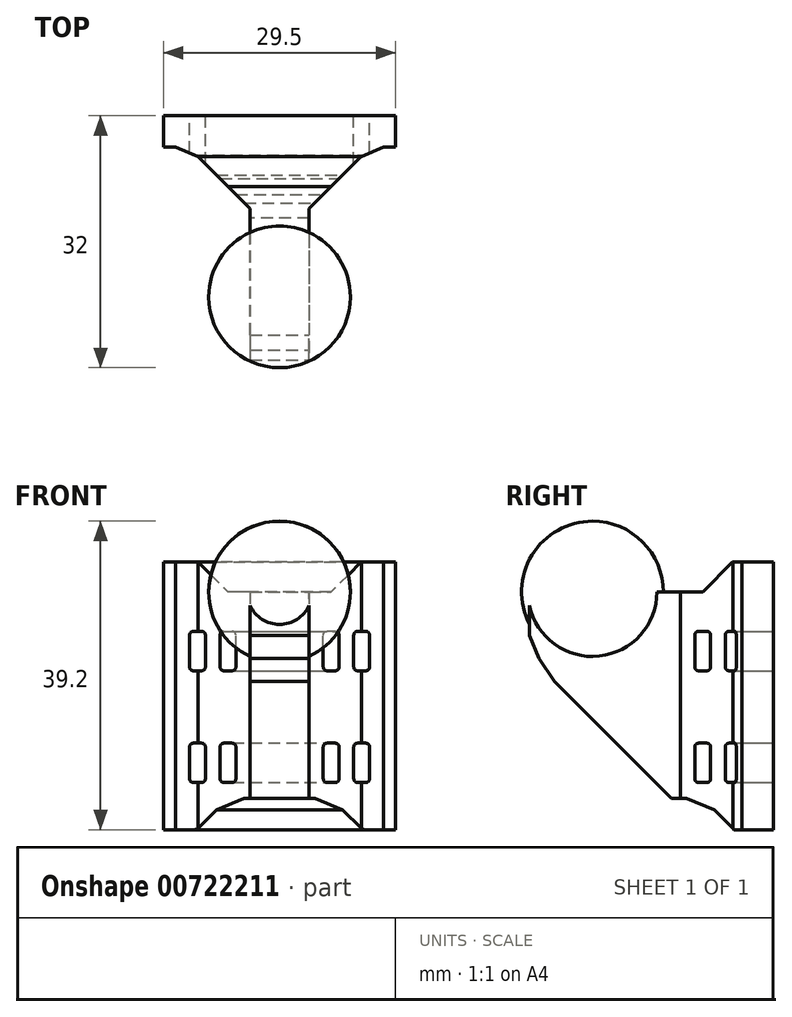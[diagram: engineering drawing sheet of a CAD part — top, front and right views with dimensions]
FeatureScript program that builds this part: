
annotation { "Feature Type Name" : "Feature", "Feature Type Description" : "" }
export const myFeature = defineFeature(function(context is Context, id is Id, definition is map)
    precondition{}
    {
        {
            var Q0;
            Q0=qCreatedBy(makeId("Top.planeOp"),FACE);
            var sketch = newSketch(context, id + "F0", { "sketchPlane" : qUnion([Q0])});
            skLineSegment(sketch, "E0", {"start": v(-34.8, 0) * mm, "end": v(28.46, 0) * mm, "construction": true});
            skArc(sketch, "E1", {"start": v(9, 0) * mm, "mid": v(0, 9) * mm, "end": v(-9, 0) * mm});
            skLineSegment(sketch, "E2", {"start": v(-9, 0) * mm, "end": v(9, 0) * mm});
            skSolve(sketch);
        }
        {
            var Q0;
            Q0 = qSketchRegion(id + "F0", true);
            var Q1;
            Q1=sQuery(id+"F0.wireOp",EDGE,"E0");
            revolve(context, id + "F1", {"surfaceOperationType" : NewSurfaceOperationType.NEW, "entities" : qUnion([Q0]), "axis" : qUnion([Q1]), "revolveType" : RevolveType.FULL});
        }
        {
            var Q0;
            Q0=qCreatedBy(makeId("Front.planeOp"),FACE);
            var sketch = newSketch(context, id + "F2", { "sketchPlane" : qUnion([Q0])});
            skLineSegment(sketch, "E3.bottom", {"start": v(-3.75, 0) * mm, "end": v(3.75, 0) * mm});
            skLineSegment(sketch, "E3.top", {"start": v(-3.75, -26.2) * mm, "end": v(3.75, -26.2) * mm});
            skLineSegment(sketch, "E3.left", {"start": v(-3.75, 0) * mm, "end": v(-3.75, -26.2) * mm});
            skLineSegment(sketch, "E3.right", {"start": v(3.75, 0) * mm, "end": v(3.75, -26.2) * mm});
            skPoint(sketch, "E3.middle", {"position": v(0, -13.1) * mm});
            skSolve(sketch);
        }
        {
            var Q0;
            Q0 = qSketchRegion(id + "F2", true);
            extrude(context, id + "F3", {"entities" : qUnion([Q0]), "operationType" : NewBodyOperationType.ADD, "oppositeDirection" : true, "depth" : 19 * mm, "offsetDistance" : 25 * mm, "hasSecondDirection" : true, "secondDirectionOppositeDirection" : false, "secondDirectionDepth" : 8 * mm});
        }
        {
            var Q0;
            {var subQ0=sQuery(id+"F2.wireOp",EDGE,"E3.top");Q0=makeQuery(id+"F11.opBoolean","MERGE",FACE,{"derivedFrom":[makeQuery(id+"F3.opExtrude","SWEPT_FACE",FACE,{"disambiguationData":[OSD([subQ0])]}),makeQuery(id+"F7.opExtrude","SWEPT_FACE",FACE,{"disambiguationData":[OSD([subQ0])]}),makeQuery(id+"F9.opExtrude","SWEPT_FACE",FACE,{"disambiguationData":[OSD([subQ0,sQuery(id+"F2.wireOp",EDGE,"E3.left")])]}),makeQuery(id+"F10.opExtrude","SWEPT_FACE",FACE,{"disambiguationData":[OSD([subQ0,sQuery(id+"F2.wireOp",EDGE,"E3.right")])]})]});}
            var sketch = newSketch(context, id + "F4", { "sketchPlane" : qUnion([Q0])});
            skLineSegment(sketch, "E4", {"start": v(-14.75, -19) * mm, "end": v(14.75, -19) * mm});
            skLineSegment(sketch, "E5", {"start": v(14.75, -19) * mm, "end": v(14.75, -23) * mm});
            skLineSegment(sketch, "E6", {"start": v(14.75, -23) * mm, "end": v(-14.75, -23) * mm});
            skLineSegment(sketch, "E7", {"start": v(-14.75, -23) * mm, "end": v(-14.75, -19) * mm});
            skSolve(sketch);
        }
        {
            var Q0;
            Q0=makeQuery(id+"F3.opExtrude","CAP_EDGE",EDGE,{"disambiguationData":[OSD([sQuery(id+"F2.wireOp",EDGE,"E3.top")])],"isStart":true});
            chamfer(context, id + "F5", {"entities" : qUnion([Q0]), "width" : 18 * mm, "tangentPropagation" : true});
        }
        {
            var Q0;
            {var subQ0=sQuery(id+"F2.wireOp",EDGE,"E3.top");Q0=makeQuery(id+"F5.opChamfer","BLEND_EDGE",EDGE,{"blendedFrom":[makeQuery(id+"F3.opExtrude","CAP_EDGE",EDGE,{"disambiguationData":[OSD([subQ0])],"isStart":true}),makeQuery(id+"F3.opExtrude","CAP_FACE",FACE,{"disambiguationData":[OSD([sQuery(id+"F2.wireOp",EDGE,"E3.bottom"),subQ0,sQuery(id+"F2.wireOp",EDGE,"E3.left"),sQuery(id+"F2.wireOp",EDGE,"E3.right")])],"isStart":true})],"blendedInto":[makeQuery(id+"F3.opExtrude","CAP_FACE",FACE,{"disambiguationData":[OSD([sQuery(id+"F2.wireOp",EDGE,"E3.bottom"),subQ0,sQuery(id+"F2.wireOp",EDGE,"E3.left"),sQuery(id+"F2.wireOp",EDGE,"E3.right")])],"isStart":true})]});}
            chamfer(context, id + "F6", {"entities" : qUnion([Q0]), "width" : 6.5 * mm, "tangentPropagation" : true});
        }
        {
            var Q0;
            Q0=makeQuery(id+"F3.opExtrude","CAP_FACE",FACE,{"disambiguationData":[OSD([sQuery(id+"F2.wireOp",EDGE,"E3.bottom"),sQuery(id+"F2.wireOp",EDGE,"E3.top"),sQuery(id+"F2.wireOp",EDGE,"E3.left"),sQuery(id+"F2.wireOp",EDGE,"E3.right")])],"isStart":false});
            extrude(context, id + "F7", {"entities" : qUnion([Q0]), "depth" : 4 * mm, "offsetDistance" : 25 * mm});
        }
        {
            var Q0;
            Q0=makeQuery(id+"F7.opExtrude","CAP_EDGE",EDGE,{"disambiguationData":[OSD([sQuery(id+"F2.wireOp",EDGE,"E3.bottom")])],"isStart":false});
            chamfer(context, id + "F8", {"entities" : qUnion([Q0]), "chamferType" : ChamferType.OFFSET_ANGLE, "width" : 3 * mm, "oppositeDirection" : false, "angle" : 70 * degree, "tangentPropagation" : true});
        }
        {
            var Q0;
            Q0=makeQuery(id+"F7.opExtrude","SWEPT_FACE",FACE,{"disambiguationData":[OSD([sQuery(id+"F2.wireOp",EDGE,"E3.left")])]});
            extrude(context, id + "F9", {"entities" : qUnion([Q0]), "depth" : 11 * mm, "offsetDistance" : 25 * mm});
        }
        {
            var Q0;
            Q0=makeQuery(id+"F7.opExtrude","SWEPT_FACE",FACE,{"disambiguationData":[OSD([sQuery(id+"F2.wireOp",EDGE,"E3.right")])]});
            extrude(context, id + "F10", {"entities" : qUnion([Q0]), "depth" : 11 * mm, "offsetDistance" : 25 * mm});
        }
        {
            var Q0;
            Q0=makeQuery(id+"F1.opRevolve","SWEPT_BODY",BODY,{"disambiguationData":[OSD([sQuery(id+"F0.wireOp",EDGE,"E1"),sQuery(id+"F0.wireOp",EDGE,"E2")])]});
            var Q1;
            Q1=makeQuery(id+"F7.opExtrude","SWEPT_BODY",BODY,{"disambiguationData":[OSD([sQuery(id+"F2.wireOp",EDGE,"E3.bottom"),sQuery(id+"F2.wireOp",EDGE,"E3.top"),sQuery(id+"F2.wireOp",EDGE,"E3.left"),sQuery(id+"F2.wireOp",EDGE,"E3.right")])]});
            var Q2;
            Q2=makeQuery(id+"F10.opExtrude","SWEPT_BODY",BODY,{"disambiguationData":[OSD([sQuery(id+"F2.wireOp",EDGE,"E3.right")])]});
            var Q3;
            Q3=makeQuery(id+"FVza8cOxjJakpDc_3.opExtrude","SWEPT_BODY",BODY,{"disambiguationData":[OSD([sQuery(id+"F2.wireOp",EDGE,"E3.right")])]});
            var Q4;
            Q4=makeQuery(id+"FVza8cOxjJakpDc_3.opExtrude","SWEPT_BODY",BODY,{"disambiguationData":[OSD([sQuery(id+"F2.wireOp",EDGE,"E3.left")])]});
            var Q5;
            Q5=makeQuery(id+"F9.opExtrude","SWEPT_BODY",BODY,{"disambiguationData":[OSD([sQuery(id+"F2.wireOp",EDGE,"E3.left")])]});
            booleanBodies(context, id + "F11", {"operationType" : BooleanOperationType.UNION, "tools" : qUnion([Q0, Q1, Q2, Q3, Q4, Q5])});
        }
        {
            var Q0;
            {var subQ0=sQuery(id+"F2.wireOp",EDGE,"E3.right");var subQ1=sQuery(id+"F2.wireOp",EDGE,"E3.left");Q0=makeQuery(id+"F11.opBoolean","SPLIT",EDGE,{"disambiguationData":[topologyDisambiguationEdgeConnected([makeQuery(id+"F9.opExtrude","SWEPT_FACE",FACE,{"disambiguationData":[OSD([subQ1]),TDD([makeQuery(id+"F7.opExtrude","CAP_EDGE",EDGE,{"disambiguationData":[OSD([subQ1])],"isStart":true})])]})])],"derivedFrom":makeQuery(id+"F3.opExtrude","CAP_EDGE",EDGE,{"disambiguationData":[OSD([subQ0])],"isStart":false})});}
            var Q1;
            {var subQ0=sQuery(id+"F2.wireOp",EDGE,"E3.left");Q1=makeQuery(id+"F11.opBoolean","SPLIT",EDGE,{"disambiguationData":[topologyDisambiguationEdgeConnected([makeQuery(id+"F9.opExtrude","SWEPT_FACE",FACE,{"disambiguationData":[OSD([subQ0]),TDD([makeQuery(id+"F7.opExtrude","CAP_EDGE",EDGE,{"disambiguationData":[OSD([subQ0])],"isStart":true})])]})])],"derivedFrom":makeQuery(id+"F3.opExtrude","CAP_EDGE",EDGE,{"disambiguationData":[OSD([subQ0])],"isStart":false})});}
            chamfer(context, id + "F12", {"entities" : qUnion([Q0, Q1]), "width" : 7.8 * mm, "tangentPropagation" : true});
        }
        {
            var Q0;
            {var subQ0=sQuery(id+"F2.wireOp",EDGE,"E3.right");var subQ1=sQuery(id+"F2.wireOp",EDGE,"E3.left");Q0=makeQuery(id+"F11.opBoolean","MERGE",FACE,{"derivedFrom":[makeQuery(id+"F7.opExtrude","CAP_FACE",FACE,{"disambiguationData":[OSD([sQuery(id+"F2.wireOp",EDGE,"E3.bottom"),sQuery(id+"F2.wireOp",EDGE,"E3.top"),subQ1,subQ0])],"isStart":false}),makeQuery(id+"F9.opExtrude","SWEPT_FACE",FACE,{"disambiguationData":[OSD([subQ1]),TDD([makeQuery(id+"F7.opExtrude","CAP_EDGE",EDGE,{"disambiguationData":[OSD([subQ1])],"isStart":false})])]}),makeQuery(id+"F10.opExtrude","SWEPT_FACE",FACE,{"disambiguationData":[OSD([subQ0]),TDD([makeQuery(id+"F7.opExtrude","CAP_EDGE",EDGE,{"disambiguationData":[OSD([subQ0])],"isStart":false})])]})]});}
            var sketch = newSketch(context, id + "F13", { "sketchPlane" : qUnion([Q0])});
            skLineSegment(sketch, "E8.bottom", {"start": v(-10.96, -5) * mm, "end": v(-9.88, -5) * mm});
            skLineSegment(sketch, "E8.top", {"start": v(-10.96, -10) * mm, "end": v(-9.88, -10) * mm});
            skLineSegment(sketch, "E8.left", {"start": v(-11.42, -5.46) * mm, "end": v(-11.42, -9.54) * mm});
            skLineSegment(sketch, "E8.right", {"start": v(-9.42, -5.46) * mm, "end": v(-9.42, -9.54) * mm});
            skLineSegment(sketch, "E9", {"start": v(-14.75, -14.6) * mm, "end": v(14.75, -14.6) * mm, "construction": true});
            skPoint(sketch, "E10.visualSharp", {"position": v(-9.42, -5) * mm});
            skArc(sketch, "E10.filletArc", {"start": v(-9.42, -5.46) * mm, "mid": v(-9.56, -5.13) * mm, "end": v(-9.88, -5) * mm});
            skPoint(sketch, "E11.visualSharp", {"position": v(-11.42, -5) * mm});
            skArc(sketch, "E11.filletArc", {"start": v(-10.96, -5) * mm, "mid": v(-11.29, -5.13) * mm, "end": v(-11.42, -5.46) * mm});
            skPoint(sketch, "E12.visualSharp", {"position": v(-9.42, -10) * mm});
            skArc(sketch, "E12.filletArc", {"start": v(-9.88, -10) * mm, "mid": v(-9.56, -9.87) * mm, "end": v(-9.42, -9.54) * mm});
            skPoint(sketch, "E13.visualSharp", {"position": v(-11.42, -10) * mm});
            skArc(sketch, "E13.filletArc", {"start": v(-11.42, -9.54) * mm, "mid": v(-11.29, -9.87) * mm, "end": v(-10.96, -10) * mm});
            skLineSegment(sketch, "E14.MirrorCS", {"start": v(-9.42, -23.74) * mm, "end": v(-9.42, -19.66) * mm});
            skArc(sketch, "E15.MirrorCS", {"start": v(-9.42, -23.74) * mm, "mid": v(-9.56, -24.07) * mm, "end": v(-9.88, -24.2) * mm});
            skLineSegment(sketch, "E16.MirrorCS", {"start": v(-10.96, -24.2) * mm, "end": v(-9.88, -24.2) * mm});
            skArc(sketch, "E17.MirrorCS", {"start": v(-10.96, -24.2) * mm, "mid": v(-11.29, -24.07) * mm, "end": v(-11.42, -23.74) * mm});
            skLineSegment(sketch, "E18.MirrorCS", {"start": v(-11.42, -23.74) * mm, "end": v(-11.42, -19.66) * mm});
            skArc(sketch, "E19.MirrorCS", {"start": v(-11.42, -19.66) * mm, "mid": v(-11.29, -19.33) * mm, "end": v(-10.96, -19.2) * mm});
            skLineSegment(sketch, "E20.MirrorCS", {"start": v(-10.96, -19.2) * mm, "end": v(-9.88, -19.2) * mm});
            skArc(sketch, "E21.MirrorCS", {"start": v(-9.88, -19.2) * mm, "mid": v(-9.56, -19.33) * mm, "end": v(-9.42, -19.66) * mm});
            skArc(sketch, "E22.MirrorCS", {"start": v(9.42, -5.46) * mm, "mid": v(9.56, -5.13) * mm, "end": v(9.88, -5) * mm});
            skLineSegment(sketch, "E23.MirrorCS", {"start": v(10.96, -5) * mm, "end": v(9.88, -5) * mm});
            skArc(sketch, "E24.MirrorCS", {"start": v(10.96, -5) * mm, "mid": v(11.29, -5.13) * mm, "end": v(11.42, -5.46) * mm});
            skLineSegment(sketch, "E25.MirrorCS", {"start": v(11.42, -5.46) * mm, "end": v(11.42, -9.54) * mm});
            skArc(sketch, "E26.MirrorCS", {"start": v(11.42, -9.54) * mm, "mid": v(11.29, -9.87) * mm, "end": v(10.96, -10) * mm});
            skLineSegment(sketch, "E27.MirrorCS", {"start": v(10.96, -10) * mm, "end": v(9.88, -10) * mm});
            skArc(sketch, "E28.MirrorCS", {"start": v(9.88, -10) * mm, "mid": v(9.56, -9.87) * mm, "end": v(9.42, -9.54) * mm});
            skLineSegment(sketch, "E29.MirrorCS", {"start": v(9.42, -5.46) * mm, "end": v(9.42, -9.54) * mm});
            skArc(sketch, "E30.MirrorCS", {"start": v(9.42, -23.74) * mm, "mid": v(9.56, -24.07) * mm, "end": v(9.88, -24.2) * mm});
            skLineSegment(sketch, "E31.MirrorCS", {"start": v(10.96, -24.2) * mm, "end": v(9.88, -24.2) * mm});
            skArc(sketch, "E32.MirrorCS", {"start": v(10.96, -24.2) * mm, "mid": v(11.29, -24.07) * mm, "end": v(11.42, -23.74) * mm});
            skLineSegment(sketch, "E33.MirrorCS", {"start": v(11.42, -23.74) * mm, "end": v(11.42, -19.66) * mm});
            skLineSegment(sketch, "E34.MirrorCS", {"start": v(9.42, -23.74) * mm, "end": v(9.42, -19.66) * mm});
            skArc(sketch, "E35.MirrorCS", {"start": v(9.88, -19.2) * mm, "mid": v(9.56, -19.33) * mm, "end": v(9.42, -19.66) * mm});
            skLineSegment(sketch, "E36.MirrorCS", {"start": v(10.96, -19.2) * mm, "end": v(9.88, -19.2) * mm});
            skArc(sketch, "E37.MirrorCS", {"start": v(11.42, -19.66) * mm, "mid": v(11.29, -19.33) * mm, "end": v(10.96, -19.2) * mm});
            skSolve(sketch);
        }
        {
            var Q0;
            Q0 = qSketchRegion(id + "F4", true);
            extrude(context, id + "F14", {"entities" : qUnion([Q0]), "operationType" : NewBodyOperationType.ADD, "depth" : 4 * mm, "offsetDistance" : 25 * mm, "hasSecondDirection" : true, "secondDirectionOppositeDirection" : true, "secondDirectionDepth" : 30 * mm});
        }
        {
            var Q0;
            Q0 = qSketchRegion(id + "F13", true);
            extrude(context, id + "F15", {"entities" : qUnion([Q0]), "operationType" : NewBodyOperationType.REMOVE, "endBound" : BoundingType.THROUGH_ALL, "oppositeDirection" : true, "depth" : 25 * mm, "offsetDistance" : 25 * mm});
        }
        {
            var Q0;
            Q0=makeQuery(id+"F3.opExtrude","SWEPT_FACE",FACE,{"disambiguationData":[OSD([sQuery(id+"F2.wireOp",EDGE,"E3.right")])]});
            var sketch = newSketch(context, id + "F16", { "sketchPlane" : qUnion([Q0])});
            skLineSegment(sketch, "E38.0", {"start": v(17, -9.54) * mm, "end": v(17, -5.46) * mm, "construction": true});
            skLineSegment(sketch, "E39.0", {"start": v(17, -19.66) * mm, "end": v(17, -23.74) * mm, "construction": true});
            skPoint(sketch, "E40.0", {"position": v(17.87, -10) * mm});
            skPoint(sketch, "E41.0", {"position": v(17.87, -5) * mm});
            skPoint(sketch, "E42.0", {"position": v(17.87, -19.2) * mm});
            skPoint(sketch, "E43.0", {"position": v(17.87, -24.2) * mm});
            skLineSegment(sketch, "E44.bottom", {"start": v(13.46, -5) * mm, "end": v(14.54, -5) * mm});
            skLineSegment(sketch, "E44.top", {"start": v(13.46, -10) * mm, "end": v(14.54, -10) * mm});
            skLineSegment(sketch, "E44.left", {"start": v(13, -5.46) * mm, "end": v(13, -9.54) * mm});
            skLineSegment(sketch, "E44.right", {"start": v(15, -5.46) * mm, "end": v(15, -9.54) * mm});
            skLineSegment(sketch, "E45.bottom", {"start": v(14.54, -19.2) * mm, "end": v(13.46, -19.2) * mm});
            skLineSegment(sketch, "E45.top", {"start": v(14.54, -24.2) * mm, "end": v(13.46, -24.2) * mm});
            skLineSegment(sketch, "E45.left", {"start": v(15, -19.66) * mm, "end": v(15, -23.74) * mm});
            skLineSegment(sketch, "E45.right", {"start": v(13, -19.66) * mm, "end": v(13, -23.74) * mm});
            skPoint(sketch, "E46.visualSharp", {"position": v(13, -5) * mm});
            skArc(sketch, "E46.filletArc", {"start": v(13.46, -5) * mm, "mid": v(13.13, -5.13) * mm, "end": v(13, -5.46) * mm});
            skPoint(sketch, "E47.visualSharp", {"position": v(15, -5) * mm});
            skArc(sketch, "E47.filletArc", {"start": v(15, -5.46) * mm, "mid": v(14.87, -5.13) * mm, "end": v(14.54, -5) * mm});
            skPoint(sketch, "E48.visualSharp", {"position": v(13, -10) * mm});
            skArc(sketch, "E48.filletArc", {"start": v(13, -9.54) * mm, "mid": v(13.13, -9.87) * mm, "end": v(13.46, -10) * mm});
            skPoint(sketch, "E49.visualSharp", {"position": v(15, -10) * mm});
            skArc(sketch, "E49.filletArc", {"start": v(14.54, -10) * mm, "mid": v(14.87, -9.87) * mm, "end": v(15, -9.54) * mm});
            skPoint(sketch, "E50.visualSharp", {"position": v(13, -19.2) * mm});
            skArc(sketch, "E50.filletArc", {"start": v(13.46, -19.2) * mm, "mid": v(13.13, -19.33) * mm, "end": v(13, -19.66) * mm});
            skPoint(sketch, "E51.visualSharp", {"position": v(15, -19.2) * mm});
            skArc(sketch, "E51.filletArc", {"start": v(15, -19.66) * mm, "mid": v(14.87, -19.33) * mm, "end": v(14.54, -19.2) * mm});
            skPoint(sketch, "E52.visualSharp", {"position": v(15, -24.2) * mm});
            skArc(sketch, "E52.filletArc", {"start": v(14.54, -24.2) * mm, "mid": v(14.87, -24.07) * mm, "end": v(15, -23.74) * mm});
            skPoint(sketch, "E53.visualSharp", {"position": v(13, -24.2) * mm});
            skArc(sketch, "E53.filletArc", {"start": v(13, -23.74) * mm, "mid": v(13.13, -24.07) * mm, "end": v(13.46, -24.2) * mm});
            skSolve(sketch);
        }
        {
            var Q0;
            Q0 = qSketchRegion(id + "F16", true);
            extrude(context, id + "F17", {"entities" : qUnion([Q0]), "operationType" : NewBodyOperationType.REMOVE, "endBound" : BoundingType.THROUGH_ALL, "oppositeDirection" : true, "depth" : 25 * mm, "offsetDistance" : 25 * mm, "hasSecondDirection" : true, "secondDirectionOppositeDirection" : false, "secondDirectionDepth" : 25 * mm});
        }
        {
            var Q0;
            {var subQ0=sQuery(id+"F2.wireOp",EDGE,"E3.top");Q0=makeQuery(id+"F6.opChamfer","BLEND_EDGE",EDGE,{"blendedFrom":[makeQuery(id+"F5.opChamfer","BLEND_EDGE",EDGE,{"blendedFrom":[makeQuery(id+"F3.opExtrude","CAP_EDGE",EDGE,{"disambiguationData":[OSD([subQ0])],"isStart":true}),makeQuery(id+"F3.opExtrude","CAP_FACE",FACE,{"disambiguationData":[OSD([sQuery(id+"F2.wireOp",EDGE,"E3.bottom"),subQ0,sQuery(id+"F2.wireOp",EDGE,"E3.left"),sQuery(id+"F2.wireOp",EDGE,"E3.right")])],"isStart":true})],"blendedInto":[makeQuery(id+"F3.opExtrude","CAP_FACE",FACE,{"disambiguationData":[OSD([sQuery(id+"F2.wireOp",EDGE,"E3.bottom"),subQ0,sQuery(id+"F2.wireOp",EDGE,"E3.left"),sQuery(id+"F2.wireOp",EDGE,"E3.right")])],"isStart":true})]}),makeQuery(id+"F5.opChamfer","BLEND_FACE",FACE,{"disambiguationData":[OSD([subQ0])]})],"blendedInto":[makeQuery(id+"F5.opChamfer","BLEND_FACE",FACE,{"disambiguationData":[OSD([subQ0])]})]});}
            chamfer(context, id + "F18", {"entities" : qUnion([Q0]), "width" : 9 * mm, "tangentPropagation" : true});
        }
        {
            var Q0;
            {var subQ0=sQuery(id+"F2.wireOp",EDGE,"E3.right");var subQ1=makeQuery(id+"F10.opExtrude","SWEPT_FACE",FACE,{"disambiguationData":[OSD([subQ0]),TDD([makeQuery(id+"F7.opExtrude","CAP_EDGE",EDGE,{"disambiguationData":[OSD([subQ0])],"isStart":true})])]});var subQ2=sQuery(id+"F2.wireOp",EDGE,"E3.left");var subQ3=makeQuery(id+"F9.opExtrude","SWEPT_FACE",FACE,{"disambiguationData":[OSD([subQ2]),TDD([makeQuery(id+"F7.opExtrude","CAP_EDGE",EDGE,{"disambiguationData":[OSD([subQ2])],"isStart":true})])]});var subQ4=makeQuery(id+"F7.opExtrude","CAP_FACE",FACE,{"disambiguationData":[OSD([sQuery(id+"F2.wireOp",EDGE,"E3.bottom"),sQuery(id+"F2.wireOp",EDGE,"E3.top"),subQ2,subQ0])],"isStart":true});Q0=makeQuery(id+"F15.boolean.opBoolean","SPLIT",EDGE,{"disambiguationData":[TD([makeQuery(id+"F15.opExtrude","SWEPT_FACE",FACE,{"disambiguationData":[OSD([sQuery(id+"F13.wireOp",EDGE,"E8.top")])]})])],"derivedFrom":makeQuery(id+"F12.opChamfer","BLEND_EDGE",EDGE,{"blendedFrom":[makeQuery(id+"F3.opExtrude","CAP_EDGE",EDGE,{"disambiguationData":[OSD([subQ0])],"isStart":false}),makeQuery(id+"F11.opBoolean","MERGE",FACE,{"disambiguationData":[OD(1.0)],"derivedFrom":[subQ4,subQ3,subQ1]})],"blendedInto":[makeQuery(id+"F11.opBoolean","MERGE",FACE,{"disambiguationData":[OD(1.0)],"derivedFrom":[subQ4,subQ3,subQ1]})]})});}
            var Q1;
            {var subQ0=sQuery(id+"F2.wireOp",EDGE,"E3.left");var subQ1=sQuery(id+"F2.wireOp",EDGE,"E3.right");var subQ2=makeQuery(id+"F10.opExtrude","SWEPT_FACE",FACE,{"disambiguationData":[OSD([subQ1]),TDD([makeQuery(id+"F7.opExtrude","CAP_EDGE",EDGE,{"disambiguationData":[OSD([subQ1])],"isStart":true})])]});var subQ3=makeQuery(id+"F9.opExtrude","SWEPT_FACE",FACE,{"disambiguationData":[OSD([subQ0]),TDD([makeQuery(id+"F7.opExtrude","CAP_EDGE",EDGE,{"disambiguationData":[OSD([subQ0])],"isStart":true})])]});var subQ4=makeQuery(id+"F7.opExtrude","CAP_FACE",FACE,{"disambiguationData":[OSD([sQuery(id+"F2.wireOp",EDGE,"E3.bottom"),sQuery(id+"F2.wireOp",EDGE,"E3.top"),subQ0,subQ1])],"isStart":true});Q1=makeQuery(id+"F15.boolean.opBoolean","SPLIT",EDGE,{"disambiguationData":[TD([makeQuery(id+"F15.opExtrude","SWEPT_FACE",FACE,{"disambiguationData":[OSD([sQuery(id+"F13.wireOp",EDGE,"E27.MirrorCS")])]})])],"derivedFrom":makeQuery(id+"F12.opChamfer","BLEND_EDGE",EDGE,{"blendedFrom":[makeQuery(id+"F3.opExtrude","CAP_EDGE",EDGE,{"disambiguationData":[OSD([subQ0])],"isStart":false}),makeQuery(id+"F11.opBoolean","MERGE",FACE,{"disambiguationData":[OD(0.0)],"derivedFrom":[subQ4,subQ3,subQ2]})],"blendedInto":[makeQuery(id+"F11.opBoolean","MERGE",FACE,{"disambiguationData":[OD(0.0)],"derivedFrom":[subQ4,subQ3,subQ2]})]})});}
            chamfer(context, id + "F19", {"entities" : qUnion([Q0, Q1]), "width" : 4 * mm, "tangentPropagation" : true});
        }
        {
            var Q0;
            {var subQ0=sQuery(id+"F2.wireOp",EDGE,"E3.top");Q0=makeQuery(id+"F14.boolean.opBoolean","INTERSECT",EDGE,{"derivedFrom":[makeQuery(id+"F11.opBoolean","MERGE",FACE,{"derivedFrom":[makeQuery(id+"F3.opExtrude","SWEPT_FACE",FACE,{"disambiguationData":[OSD([subQ0])]}),makeQuery(id+"F7.opExtrude","SWEPT_FACE",FACE,{"disambiguationData":[OSD([subQ0])]}),makeQuery(id+"F9.opExtrude","SWEPT_FACE",FACE,{"disambiguationData":[OSD([subQ0,sQuery(id+"F2.wireOp",EDGE,"E3.left")])]}),makeQuery(id+"F10.opExtrude","SWEPT_FACE",FACE,{"disambiguationData":[OSD([subQ0,sQuery(id+"F2.wireOp",EDGE,"E3.right")])]})]}),makeQuery(id+"F14.opExtrude","SWEPT_FACE",FACE,{"disambiguationData":[OSD([sQuery(id+"F4.wireOp",EDGE,"E4")])]})]});}
            var Q1;
            Q1=makeQuery(id+"F3.opExtrude","CAP_EDGE",EDGE,{"disambiguationData":[OSD([sQuery(id+"F2.wireOp",EDGE,"E3.bottom")])],"isStart":false});
            chamfer(context, id + "F20", {"entities" : qUnion([Q0, Q1]), "width" : 5 * mm, "tangentPropagation" : true});
        }
        {
            var Q0;
            {var subQ0=sQuery(id+"F2.wireOp",EDGE,"E3.top");var subQ1=makeQuery(id+"F11.opBoolean","MERGE",FACE,{"derivedFrom":[makeQuery(id+"F3.opExtrude","SWEPT_FACE",FACE,{"disambiguationData":[OSD([subQ0])]}),makeQuery(id+"F7.opExtrude","SWEPT_FACE",FACE,{"disambiguationData":[OSD([subQ0])]}),makeQuery(id+"F9.opExtrude","SWEPT_FACE",FACE,{"disambiguationData":[OSD([subQ0,sQuery(id+"F2.wireOp",EDGE,"E3.left")])]}),makeQuery(id+"F10.opExtrude","SWEPT_FACE",FACE,{"disambiguationData":[OSD([subQ0,sQuery(id+"F2.wireOp",EDGE,"E3.right")])]})]});Q0=makeQuery(id+"F20.opChamfer","BLEND_EDGE",EDGE,{"blendedFrom":[makeQuery(id+"F14.boolean.opBoolean","INTERSECT",EDGE,{"derivedFrom":[subQ1,makeQuery(id+"F14.opExtrude","SWEPT_FACE",FACE,{"disambiguationData":[OSD([sQuery(id+"F4.wireOp",EDGE,"E4")])]})]}),subQ1],"blendedInto":[subQ1]});}
            chamfer(context, id + "F21", {"entities" : qUnion([Q0]), "width" : 5 * mm, "tangentPropagation" : true});
        }
    });
